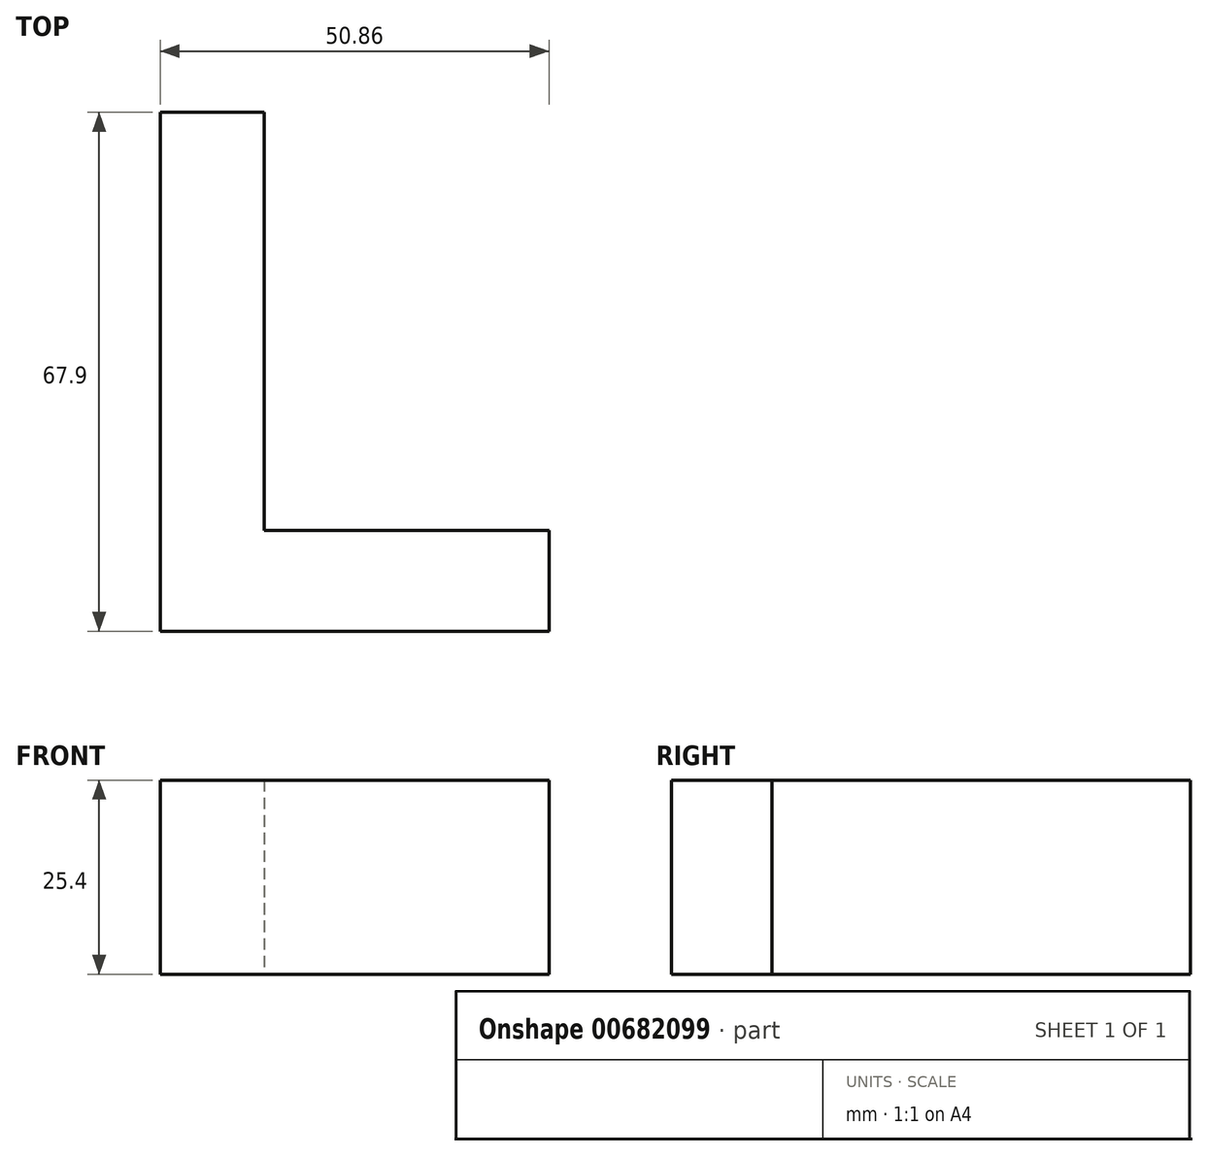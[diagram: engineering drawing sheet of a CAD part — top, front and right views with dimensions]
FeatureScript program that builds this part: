
annotation { "Feature Type Name" : "Feature", "Feature Type Description" : "" }
export const myFeature = defineFeature(function(context is Context, id is Id, definition is map)
    precondition{}
    {
        {
            var Q0;
            Q0=qCreatedBy(makeId("Top.planeOp"),FACE);
            var sketch = newSketch(context, id + "F0", { "sketchPlane" : qUnion([Q0])});
            skLineSegment(sketch, "E0", {"start": v(-57.94, 18.56) * mm, "end": v(-57.94, -32.53) * mm});
            skLineSegment(sketch, "E1", {"start": v(-57.94, -32.53) * mm, "end": v(-7.08, -32.53) * mm});
            skLineSegment(sketch, "E2", {"start": v(-7.08, -32.53) * mm, "end": v(-7.08, -19.36) * mm});
            skLineSegment(sketch, "E3", {"start": v(-7.08, -19.36) * mm, "end": v(-44.32, -19.36) * mm});
            skLineSegment(sketch, "E4", {"start": v(-44.32, -19.36) * mm, "end": v(-44.32, 18.79) * mm});
            skLineSegment(sketch, "E5", {"start": v(-44.32, 18.79) * mm, "end": v(-44.32, 35.37) * mm});
            skLineSegment(sketch, "E6", {"start": v(-44.32, 35.37) * mm, "end": v(-57.94, 35.37) * mm});
            skLineSegment(sketch, "E7", {"start": v(-57.94, 35.37) * mm, "end": v(-57.94, 18.56) * mm});
            skSolve(sketch);
        }
        {
            var Q0;
            Q0 = qSketchRegion(id + "F0", true);
            extrude(context, id + "F1", {"entities" : qUnion([Q0]), "depth" : 25.4 * mm, "offsetDistance" : 25.4 * mm});
        }
    });
